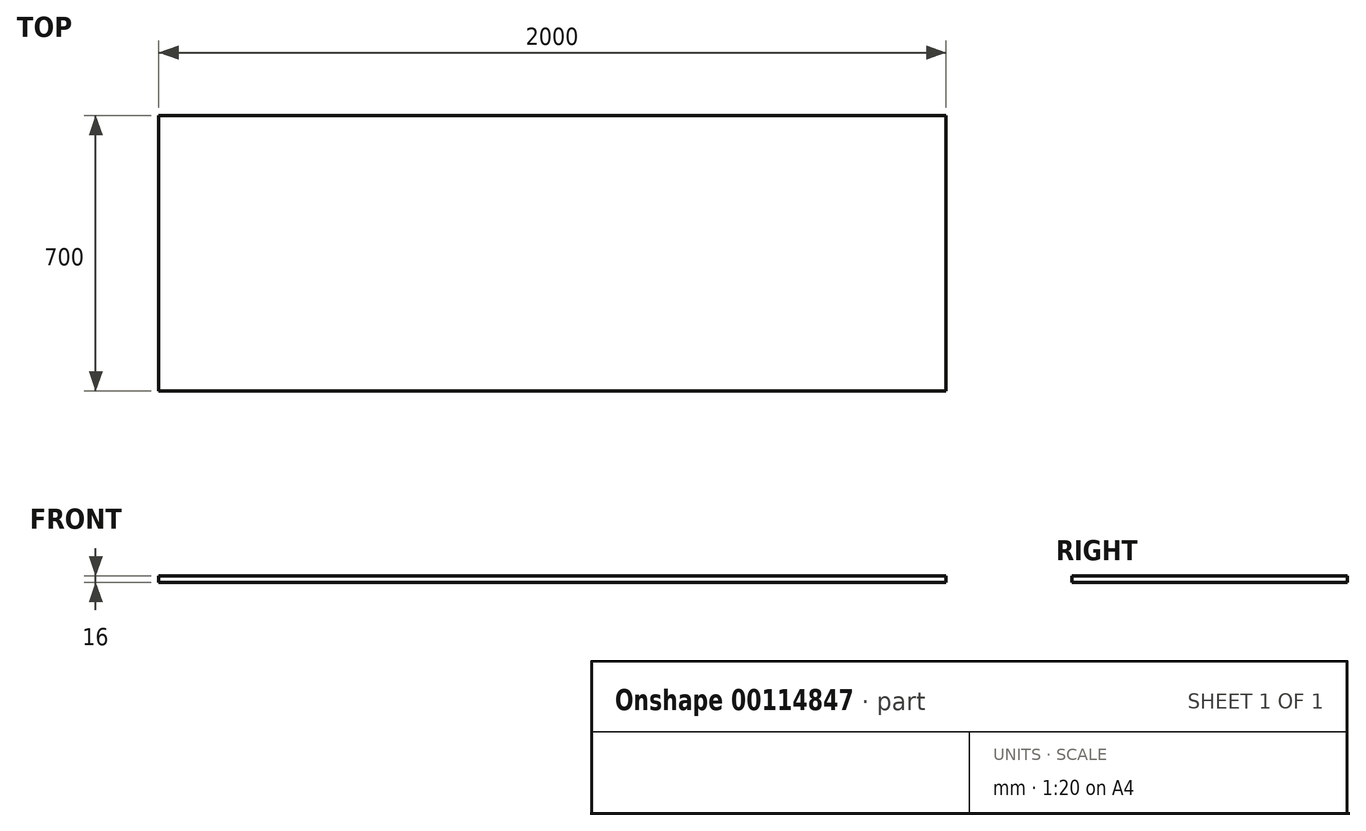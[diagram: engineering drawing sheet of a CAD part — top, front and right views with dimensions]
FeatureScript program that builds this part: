
annotation { "Feature Type Name" : "Feature", "Feature Type Description" : "" }
export const myFeature = defineFeature(function(context is Context, id is Id, definition is map)
    precondition{}
    {
        {
            var Q0;
            Q0=qCreatedBy(makeId("Top.planeOp"),FACE);
            var sketch = newSketch(context, id + "F0", { "sketchPlane" : qUnion([Q0])});
            skLineSegment(sketch, "E0.bottom", {"start": v(-1000, 350) * mm, "end": v(1000, 350) * mm});
            skLineSegment(sketch, "E0.top", {"start": v(-1000, -350) * mm, "end": v(1000, -350) * mm});
            skLineSegment(sketch, "E0.left", {"start": v(-1000, 350) * mm, "end": v(-1000, -350) * mm});
            skLineSegment(sketch, "E0.right", {"start": v(1000, 350) * mm, "end": v(1000, -350) * mm});
            skPoint(sketch, "E0.middle", {"position": v(0, 0) * mm});
            skSolve(sketch);
        }
        {
            var Q0;
            Q0=makeQuery(id+"F0.imprint","IMPRINT",FACE,{"disambiguationData":[TD([[makeQuery(id+"F0.imprint","IMPRINT",EDGE,{"derivedFrom":sQuery(id+"F0.wireOp",EDGE,"E0.bottom")}),-1.0]])]});
            extrude(context, id + "F1", {"entities" : qUnion([Q0]), "endBound" : BoundingType.SYMMETRIC, "depth" : 16 * mm});
        }
    });
